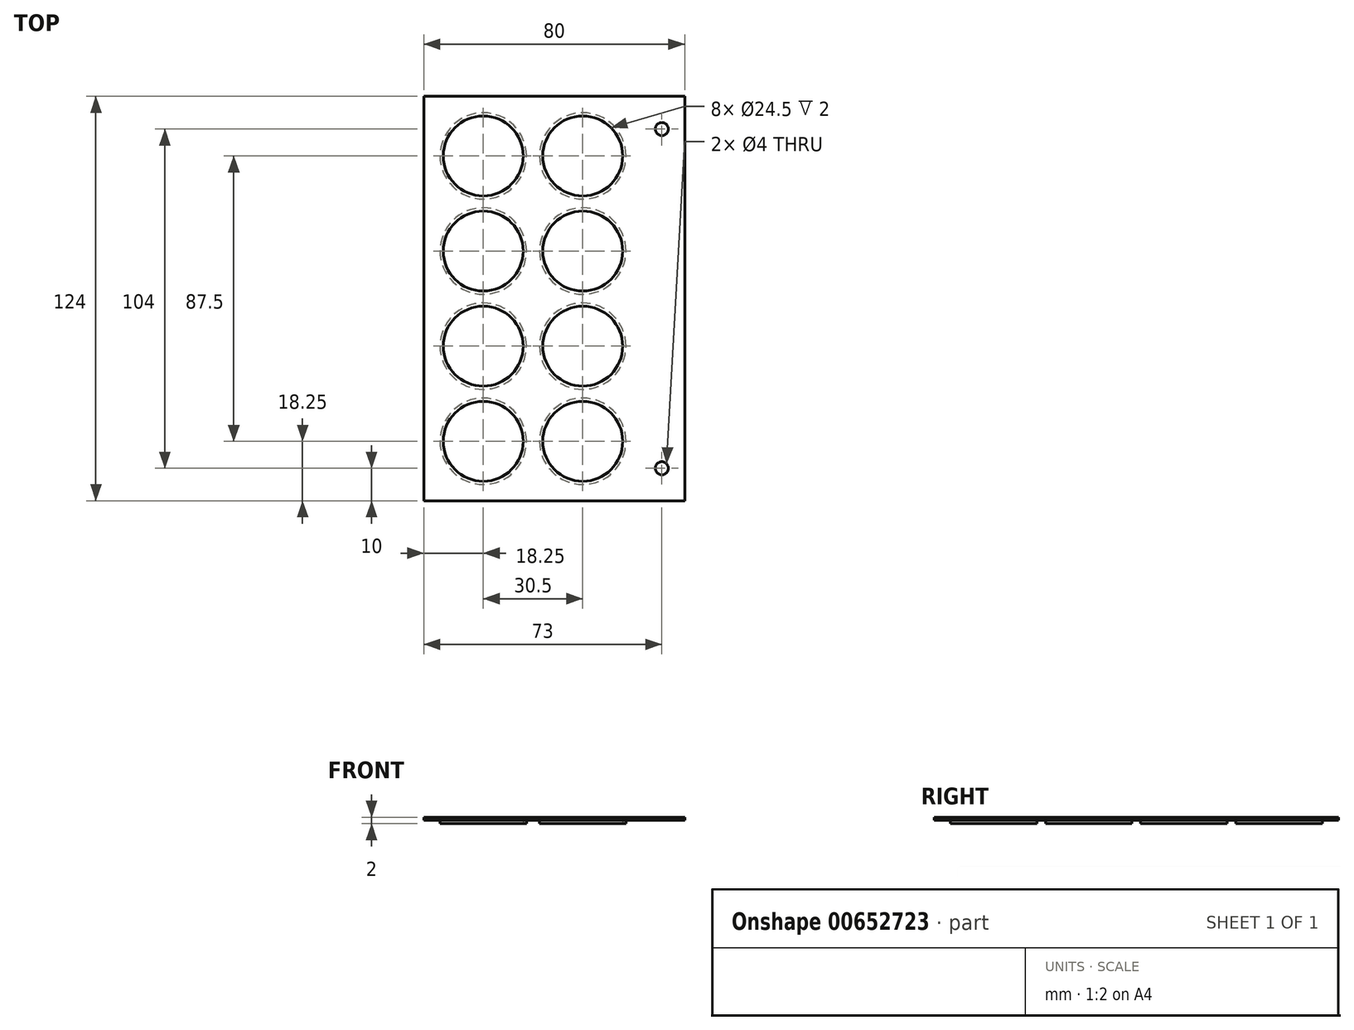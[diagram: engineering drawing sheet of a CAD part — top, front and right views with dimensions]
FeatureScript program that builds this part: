
annotation { "Feature Type Name" : "Feature", "Feature Type Description" : "" }
export const myFeature = defineFeature(function(context is Context, id is Id, definition is map)
    precondition{}
    {
        {
            var Q0;
            Q0=qCreatedBy(makeId("Top.planeOp"),FACE);
            var sketch = newSketch(context, id + "F0", { "sketchPlane" : qUnion([Q0])});
            skLineSegment(sketch, "E0.bottom", {"start": v(-40, -62) * mm, "end": v(40, -62) * mm});
            skLineSegment(sketch, "E0.top", {"start": v(-40, 62) * mm, "end": v(40, 62) * mm});
            skLineSegment(sketch, "E0.left", {"start": v(-40, -62) * mm, "end": v(-40, 62) * mm});
            skLineSegment(sketch, "E0.right", {"start": v(40, -62) * mm, "end": v(40, 62) * mm});
            skCircle(sketch, "E1", {"center": v(-21.75, 43.75) * mm, "radius": 12.25 * mm});
            skCircle(sketch, "E2.1.0.0", {"center": v(-21.75, 14.58) * mm, "radius": 12.25 * mm});
            skCircle(sketch, "E2.2.0.0", {"center": v(-21.75, -14.58) * mm, "radius": 12.25 * mm});
            skCircle(sketch, "E2.3.0.0", {"center": v(-21.75, -43.75) * mm, "radius": 12.25 * mm});
            skLineSegment(sketch, "E2.direction1", {"start": v(-21.75, 43.75) * mm, "end": v(-21.75, 14.58) * mm, "construction": true});
            skCircle(sketch, "E3.1.0.0", {"center": v(8.75, 43.75) * mm, "radius": 12.25 * mm});
            skCircle(sketch, "E3.1.0.1", {"center": v(8.75, 14.58) * mm, "radius": 12.25 * mm});
            skCircle(sketch, "E3.1.0.2", {"center": v(8.75, -14.58) * mm, "radius": 12.25 * mm});
            skCircle(sketch, "E3.1.0.3", {"center": v(8.75, -43.75) * mm, "radius": 12.25 * mm});
            skLineSegment(sketch, "E3.direction1", {"start": v(-21.75, -43.75) * mm, "end": v(8.75, -43.75) * mm, "construction": true});
            skCircle(sketch, "E4.0", {"center": v(-21.75, 43.75) * mm, "radius": 13.25 * mm});
            skCircle(sketch, "E5.0", {"center": v(-21.75, 14.58) * mm, "radius": 13.25 * mm});
            skCircle(sketch, "E6.0", {"center": v(-21.75, -14.58) * mm, "radius": 13.25 * mm});
            skCircle(sketch, "E7.0", {"center": v(-21.75, -43.75) * mm, "radius": 13.25 * mm});
            skCircle(sketch, "E8.0", {"center": v(8.75, 43.75) * mm, "radius": 13.25 * mm});
            skCircle(sketch, "E9.0", {"center": v(8.75, 14.58) * mm, "radius": 13.25 * mm});
            skCircle(sketch, "E10.0", {"center": v(8.75, -14.58) * mm, "radius": 13.25 * mm});
            skCircle(sketch, "E11.0", {"center": v(8.75, -43.75) * mm, "radius": 13.25 * mm});
            skSolve(sketch);
        }
        {
            var Q0;
            Q0=qCreatedBy(makeId("Right.planeOp"),FACE);
            var sketch = newSketch(context, id + "F1", { "sketchPlane" : qUnion([Q0])});
            skLineSegment(sketch, "E12", {"start": v(62, 0) * mm, "end": v(62, -1) * mm});
            skLineSegment(sketch, "E13", {"start": v(62, -1) * mm, "end": v(62, -2) * mm});
            skSolve(sketch);
        }
        {
            var Q0;
            Q0=makeQuery(id+"F0.imprint","IMPRINT",FACE,{"disambiguationData":[TD([[makeQuery(id+"F0.imprint","IMPRINT",EDGE,{"derivedFrom":sQuery(id+"F0.wireOp",EDGE,"E0.bottom")}),1.0]])]});
            var Q1;
            Q1=sQuery(id+"F1.wireOp",EDGE,"E12");
            sweep(context, id + "F2", {"profiles" : qUnion([Q0]), "path" : qUnion([Q1])});
        }
        {
            var Q0;
            Q0=makeQuery(id+"F0.imprint","IMPRINT",FACE,{"disambiguationData":[TD([[makeQuery(id+"F0.imprint","IMPRINT",EDGE,{"derivedFrom":sQuery(id+"F0.wireOp",EDGE,"E2.2.0.0")}),-1.0]])]});
            var Q1;
            Q1=makeQuery(id+"F0.imprint","IMPRINT",FACE,{"disambiguationData":[TD([[makeQuery(id+"F0.imprint","IMPRINT",EDGE,{"derivedFrom":sQuery(id+"F0.wireOp",EDGE,"E2.1.0.0")}),-1.0]])]});
            var Q2;
            Q2=makeQuery(id+"F0.imprint","IMPRINT",FACE,{"disambiguationData":[TD([[makeQuery(id+"F0.imprint","IMPRINT",EDGE,{"derivedFrom":sQuery(id+"F0.wireOp",EDGE,"E2.3.0.0")}),-1.0]])]});
            var Q3;
            Q3=makeQuery(id+"F0.imprint","IMPRINT",FACE,{"disambiguationData":[TD([[makeQuery(id+"F0.imprint","IMPRINT",EDGE,{"derivedFrom":sQuery(id+"F0.wireOp",EDGE,"E3.1.0.3")}),-1.0]])]});
            var Q4;
            Q4=makeQuery(id+"F0.imprint","IMPRINT",FACE,{"disambiguationData":[TD([[makeQuery(id+"F0.imprint","IMPRINT",EDGE,{"derivedFrom":sQuery(id+"F0.wireOp",EDGE,"E3.1.0.2")}),-1.0]])]});
            var Q5;
            Q5=makeQuery(id+"F0.imprint","IMPRINT",FACE,{"disambiguationData":[TD([[makeQuery(id+"F0.imprint","IMPRINT",EDGE,{"derivedFrom":sQuery(id+"F0.wireOp",EDGE,"E3.1.0.1")}),-1.0]])]});
            var Q6;
            Q6=makeQuery(id+"F0.imprint","IMPRINT",FACE,{"disambiguationData":[TD([[makeQuery(id+"F0.imprint","IMPRINT",EDGE,{"derivedFrom":sQuery(id+"F0.wireOp",EDGE,"E3.1.0.0")}),-1.0]])]});
            var Q7;
            Q7=makeQuery(id+"F0.imprint","IMPRINT",FACE,{"disambiguationData":[TD([[makeQuery(id+"F0.imprint","IMPRINT",EDGE,{"derivedFrom":sQuery(id+"F0.wireOp",EDGE,"E1")}),-1.0]])]});
            var Q8;
            Q8=sQuery(id+"F1.wireOp",EDGE,"E12");
            var Q9;
            Q9=sQuery(id+"F1.wireOp",EDGE,"E13");
            sweep(context, id + "F3", {"operationType" : NewBodyOperationType.ADD, "profiles" : qUnion([Q0, Q1, Q2, Q3, Q4, Q5, Q6, Q7]), "path" : qUnion([Q8, Q9])});
        }
        {
            var Q0;
            {var subQ0=sQuery(id+"F1.wireOp",VERTEX,"E12.start");var subQ1=sQuery(id+"F0.wireOp",EDGE,"E11.0");var subQ2=sQuery(id+"F0.wireOp",EDGE,"E10.0");var subQ3=sQuery(id+"F0.wireOp",EDGE,"E9.0");var subQ4=sQuery(id+"F0.wireOp",EDGE,"E8.0");var subQ5=sQuery(id+"F0.wireOp",EDGE,"E7.0");var subQ6=sQuery(id+"F0.wireOp",EDGE,"E6.0");var subQ7=sQuery(id+"F0.wireOp",EDGE,"E5.0");var subQ8=sQuery(id+"F0.wireOp",EDGE,"E4.0");Q0=makeQuery(id+"F3.boolean.opBoolean","MERGE",FACE,{"derivedFrom":[makeQuery(id+"F2.opSweep","CAP_FACE",FACE,{"disambiguationData":[OSD([sQuery(id+"F0.wireOp",EDGE,"E0.bottom"),sQuery(id+"F0.wireOp",EDGE,"E0.top"),sQuery(id+"F0.wireOp",EDGE,"E0.left"),sQuery(id+"F0.wireOp",EDGE,"E0.right"),subQ8,subQ7,subQ6,subQ5,subQ4,subQ3,subQ2,subQ1,subQ0])],"isStart":true}),makeQuery(id+"F3.opSweep","CAP_FACE",FACE,{"disambiguationData":[OSD([sQuery(id+"F0.wireOp",EDGE,"E1"),subQ8,subQ0])],"isStart":true}),makeQuery(id+"F3.opSweep","CAP_FACE",FACE,{"disambiguationData":[OSD([sQuery(id+"F0.wireOp",EDGE,"E2.1.0.0"),subQ7,subQ0])],"isStart":true}),makeQuery(id+"F3.opSweep","CAP_FACE",FACE,{"disambiguationData":[OSD([sQuery(id+"F0.wireOp",EDGE,"E2.2.0.0"),subQ6,subQ0])],"isStart":true}),makeQuery(id+"F3.opSweep","CAP_FACE",FACE,{"disambiguationData":[OSD([sQuery(id+"F0.wireOp",EDGE,"E2.3.0.0"),subQ5,subQ0])],"isStart":true}),makeQuery(id+"F3.opSweep","CAP_FACE",FACE,{"disambiguationData":[OSD([sQuery(id+"F0.wireOp",EDGE,"E3.1.0.0"),subQ4,subQ0])],"isStart":true}),makeQuery(id+"F3.opSweep","CAP_FACE",FACE,{"disambiguationData":[OSD([sQuery(id+"F0.wireOp",EDGE,"E3.1.0.1"),subQ3,subQ0])],"isStart":true}),makeQuery(id+"F3.opSweep","CAP_FACE",FACE,{"disambiguationData":[OSD([sQuery(id+"F0.wireOp",EDGE,"E3.1.0.2"),subQ2,subQ0])],"isStart":true}),makeQuery(id+"F3.opSweep","CAP_FACE",FACE,{"disambiguationData":[OSD([sQuery(id+"F0.wireOp",EDGE,"E3.1.0.3"),subQ1,subQ0])],"isStart":true})]});}
            var sketch = newSketch(context, id + "F4", { "sketchPlane" : qUnion([Q0])});
            skCircle(sketch, "E14", {"center": v(33, 52) * mm, "radius": 2 * mm});
            skCircle(sketch, "E15.1.0.0", {"center": v(33, -52) * mm, "radius": 2 * mm});
            skSolve(sketch);
        }
        {
            var Q0;
            Q0=makeQuery(id+"F4.imprint","IMPRINT",FACE,{"disambiguationData":[TD([[makeQuery(id+"F4.imprint","IMPRINT",EDGE,{"derivedFrom":sQuery(id+"F4.wireOp",EDGE,"E14")}),1.0]])]});
            var Q1;
            Q1=makeQuery(id+"F4.imprint","IMPRINT",FACE,{"disambiguationData":[TD([[makeQuery(id+"F4.imprint","IMPRINT",EDGE,{"derivedFrom":sQuery(id+"F4.wireOp",EDGE,"E15.1.0.0")}),1.0]])]});
            extrude(context, id + "F5", {"entities" : qUnion([Q0, Q1]), "operationType" : NewBodyOperationType.REMOVE, "oppositeDirection" : true, "depth" : 2 * mm, "offsetDistance" : 25 * mm});
        }
    });
